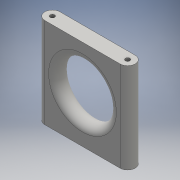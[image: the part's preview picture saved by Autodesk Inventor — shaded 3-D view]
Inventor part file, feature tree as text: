
AUTODESK INVENTOR PART (.ipt)
format: ipt  version: 2016 (Build 200138000, 138)  size: 146,432 bytes
history: native  units: mm
features: extrude x2, sketch x2, fillet x1
ambient origin geometry x8: Origin, YZ Plane, XZ Plane, XY Plane, X Axis, Y Axis, Z Axis, Center Point
bodies: Solid1 (feature_tree)
feature tree (5):
  extrude  "Extrusion1"  Depth=10.0mm
  extrude  "Extrusion2"  Depth=5.0mm
  fillet  "Fillet1"  Radius=3.0mm
  sketch  "Sketch1"  dims[d0=60.0mm d1=10.0mm]
  sketch  "Sketch2"  dims[d2=5.0mm d3=5.0mm d4=3.0mm d5=3.0mm d6=5.0mm d7=5.0mm d8=60.0mm d9=0.0mm d10=35.0mm d12=30.0mm d13=30.863283mm d14=10.0mm d15=0.0mm d16=5.0mm]
